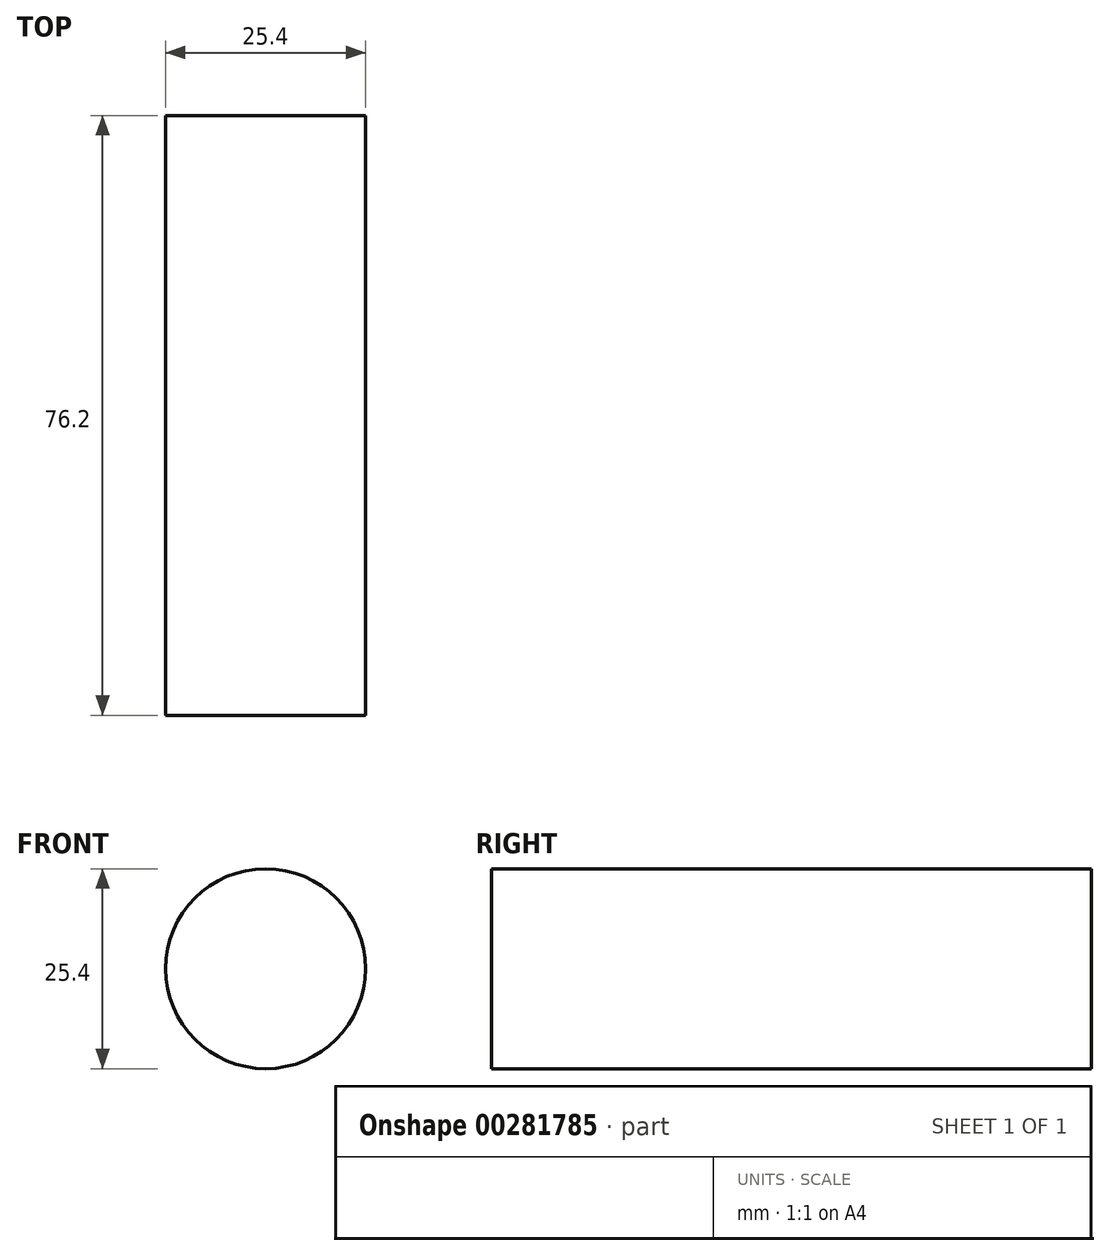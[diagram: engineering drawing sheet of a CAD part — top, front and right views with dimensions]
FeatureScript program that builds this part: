
annotation { "Feature Type Name" : "Feature", "Feature Type Description" : "" }
export const myFeature = defineFeature(function(context is Context, id is Id, definition is map)
    precondition{}
    {
        {
            var Q0;
            Q0=qCreatedBy(makeId("Front.planeOp"),FACE);
            var sketch = newSketch(context, id + "F0", { "sketchPlane" : qUnion([Q0])});
            skCircle(sketch, "E0", {"center": v(-4.38, 6.34) * mm, "radius": 12.7 * mm});
            skSolve(sketch);
        }
        {
            var Q0;
            Q0 = qSketchRegion(id + "F0", true);
            extrude(context, id + "F1", {"entities" : qUnion([Q0]), "depth" : 76.2 * mm});
        }
    });
